# Revit family: result
name_source: partatom
category: Plumbing Fixtures
revit_build: Autodesk Revit 2015 (Build: 20140903_1530(x64)
units: mm (PartAtom-declared; Revit-internal decimal feet)

## types (1)
- Default
    BIMobject category = Toilets
    BIMobject category code = sanitary-toilets
    BIMobject main category = Sanitary
    BIMobject main category code = sanitary
    Brand url = http://www.duravit.com
    Edition number = 1
    GTIN code = https://4063382012531
    IFC Classification = Sanitary Terminal
    Manufacturer name = DURAVIT
    Masterformat 2014 Code = 01 52 19
    Masterformat 2014 Description = Sanitary Facilities
    Material main = Ceramics
    NBS Reference Code = 35-65-90
    NBS Reference Description = Toilet Systems
    OmniClass Code = 23-31 19 00
    OmniClass Description = Toilets
    Product Guid = 024db9ae-2d72-4dba-8cb3-7b131d69466f
    Product SKU = white-tulip-floor-mounted-toilet-200109
    Product data url = https://bimobject.com
    Product family = White Tulip
    Product group = Toilet
    Product name = 200109 Floor-mounted-toilet
    Product url = https://duravit-public-assets.s3.eu-central-1.amazonaws.com
    QR code = http://bimobject.com
    UNSPSC Code = 301815
    Uniclass 1.4 Code = L7216
    Uniclass 1.4 Description = Toilets
    Uniclass 2.0 Code = SS-35-65-90
    Uniclass 2.0 Description = Toilet Systems
    Uniclass 2015 Code = Pr_40_20_93
    Uniclass 2015 Name = Urinal and WC fittings
    Uniformat II Code = D2030
    Uniformat II Description = Sanitary Waste

## geometry (parser evidence)
native form markers: Sweep x3
no freeform markers — native parametric forms only
